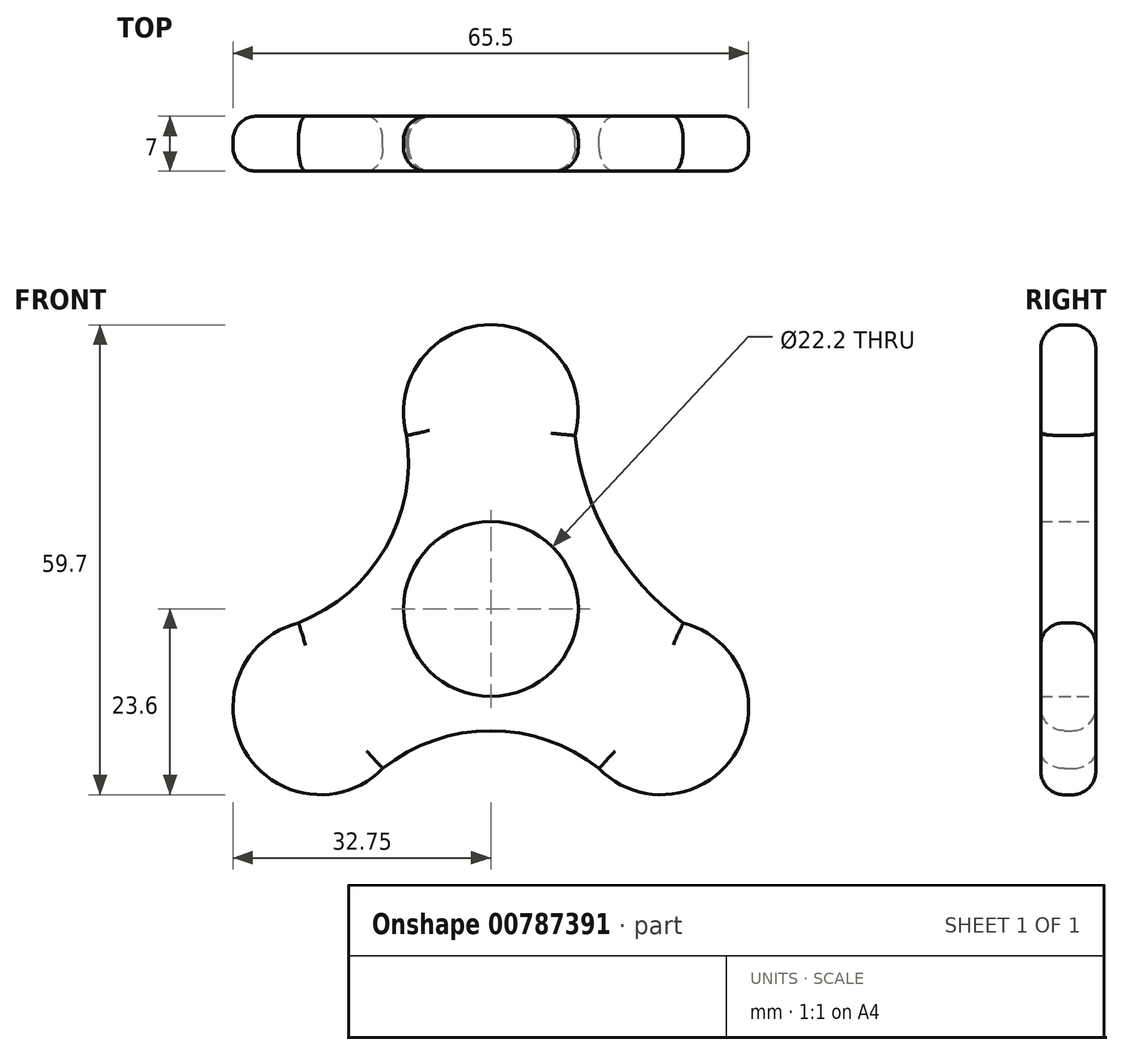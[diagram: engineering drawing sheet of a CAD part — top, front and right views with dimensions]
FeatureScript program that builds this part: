
annotation { "Feature Type Name" : "Feature", "Feature Type Description" : "" }
export const myFeature = defineFeature(function(context is Context, id is Id, definition is map)
    precondition{}
    {
        {
            var Q0;
            Q0=qCreatedBy(makeId("Front.planeOp"),FACE);
            var sketch = newSketch(context, id + "F0", { "sketchPlane" : qUnion([Q0])});
            skCircle(sketch, "E0", {"center": v(0, 0) * mm, "radius": 11.1 * mm});
            skArc(sketch, "E1", {"start": v(10.7, 22.04) * mm, "mid": v(0, 36.1) * mm, "end": v(-10.7, 22.04) * mm});
            skArc(sketch, "E2.1.0", {"start": v(-24.43, -1.75) * mm, "mid": v(-31.26, -18.05) * mm, "end": v(-13.74, -20.28) * mm});
            skArc(sketch, "E2.2.0", {"start": v(13.74, -20.28) * mm, "mid": v(31.26, -18.05) * mm, "end": v(24.43, -1.75) * mm});
            skArc(sketch, "E3", {"start": v(-24.43, -1.75) * mm, "mid": v(-13.4, 7.73) * mm, "end": v(-10.7, 22.04) * mm});
            skArc(sketch, "E4", {"start": v(10.7, 22.04) * mm, "mid": v(15.07, 8.7) * mm, "end": v(24.43, -1.75) * mm});
            skArc(sketch, "E5", {"start": v(13.74, -20.28) * mm, "mid": v(0, -15.47) * mm, "end": v(-13.74, -20.28) * mm});
            skSolve(sketch);
        }
        {
            var Q0;
            Q0 = qSketchRegion(id + "F0", true);
            extrude(context, id + "F1", {"entities" : qUnion([Q0]), "depth" : 7 * mm, "offsetDistance" : 25 * mm});
        }
        {
            var Q0;
            Q0=makeQuery(id+"F1.opExtrude","CAP_EDGE",EDGE,{"disambiguationData":[OSD([sQuery(id+"F0.wireOp",EDGE,"E2.1.0")])],"isStart":false});
            var Q1;
            Q1=makeQuery(id+"F1.opExtrude","CAP_EDGE",EDGE,{"disambiguationData":[OSD([sQuery(id+"F0.wireOp",EDGE,"E3")])],"isStart":false});
            var Q2;
            Q2=makeQuery(id+"F1.opExtrude","CAP_EDGE",EDGE,{"disambiguationData":[OSD([sQuery(id+"F0.wireOp",EDGE,"E1")])],"isStart":false});
            var Q3;
            Q3=makeQuery(id+"F1.opExtrude","CAP_EDGE",EDGE,{"disambiguationData":[OSD([sQuery(id+"F0.wireOp",EDGE,"E4")])],"isStart":false});
            var Q4;
            Q4=makeQuery(id+"F1.opExtrude","CAP_EDGE",EDGE,{"disambiguationData":[OSD([sQuery(id+"F0.wireOp",EDGE,"E2.2.0")])],"isStart":false});
            var Q5;
            Q5=makeQuery(id+"F1.opExtrude","CAP_EDGE",EDGE,{"disambiguationData":[OSD([sQuery(id+"F0.wireOp",EDGE,"E5")])],"isStart":false});
            fillet(context, id + "F2", {"entities" : qUnion([Q0, Q1, Q2, Q3, Q4, Q5]), "radius" : 3 * mm, "tangentPropagation" : true, "allowEdgeOverflow" : false});
        }
        {
            var Q0;
            Q0=makeQuery(id+"F1.opExtrude","CAP_EDGE",EDGE,{"disambiguationData":[OSD([sQuery(id+"F0.wireOp",EDGE,"E2.1.0")])],"isStart":true});
            var Q1;
            Q1=makeQuery(id+"F1.opExtrude","CAP_EDGE",EDGE,{"disambiguationData":[OSD([sQuery(id+"F0.wireOp",EDGE,"E5")])],"isStart":true});
            var Q2;
            Q2=makeQuery(id+"F1.opExtrude","CAP_EDGE",EDGE,{"disambiguationData":[OSD([sQuery(id+"F0.wireOp",EDGE,"E2.2.0")])],"isStart":true});
            var Q3;
            Q3=makeQuery(id+"F1.opExtrude","CAP_EDGE",EDGE,{"disambiguationData":[OSD([sQuery(id+"F0.wireOp",EDGE,"E1")])],"isStart":true});
            var Q4;
            Q4=makeQuery(id+"F1.opExtrude","CAP_EDGE",EDGE,{"disambiguationData":[OSD([sQuery(id+"F0.wireOp",EDGE,"E4")])],"isStart":true});
            var Q5;
            Q5=makeQuery(id+"F1.opExtrude","CAP_EDGE",EDGE,{"disambiguationData":[OSD([sQuery(id+"F0.wireOp",EDGE,"E3")])],"isStart":true});
            fillet(context, id + "F3", {"entities" : qUnion([Q0, Q1, Q2, Q3, Q4, Q5]), "radius" : 3 * mm, "tangentPropagation" : true, "allowEdgeOverflow" : false});
        }
        {
            var Q0;
            Q0=qCreatedBy(makeId("Front.planeOp"),FACE);
            var sketch = newSketch(context, id + "F4", { "sketchPlane" : qUnion([Q0])});
            skText(sketch, "E6", { "text": "tw", "fontName": "OpenSans-Bold.ttf"});
            const initialGuessF4  = {"E6": [-0.00395, 0.02028, 1, 0, 0.00504]};
            skSetInitialGuess(sketch, initialGuessF4);
            skSolve(sketch);
        }
        {
            var Q0;
            Q0 = qSketchRegion(id + "F4", true);
            extrude(context, id + "F5", {"entities" : qUnion([Q0]), "operationType" : NewBodyOperationType.REMOVE, "oppositeDirection" : true, "depth" : 1 * mm, "offsetDistance" : 25 * mm});
        }
    });
